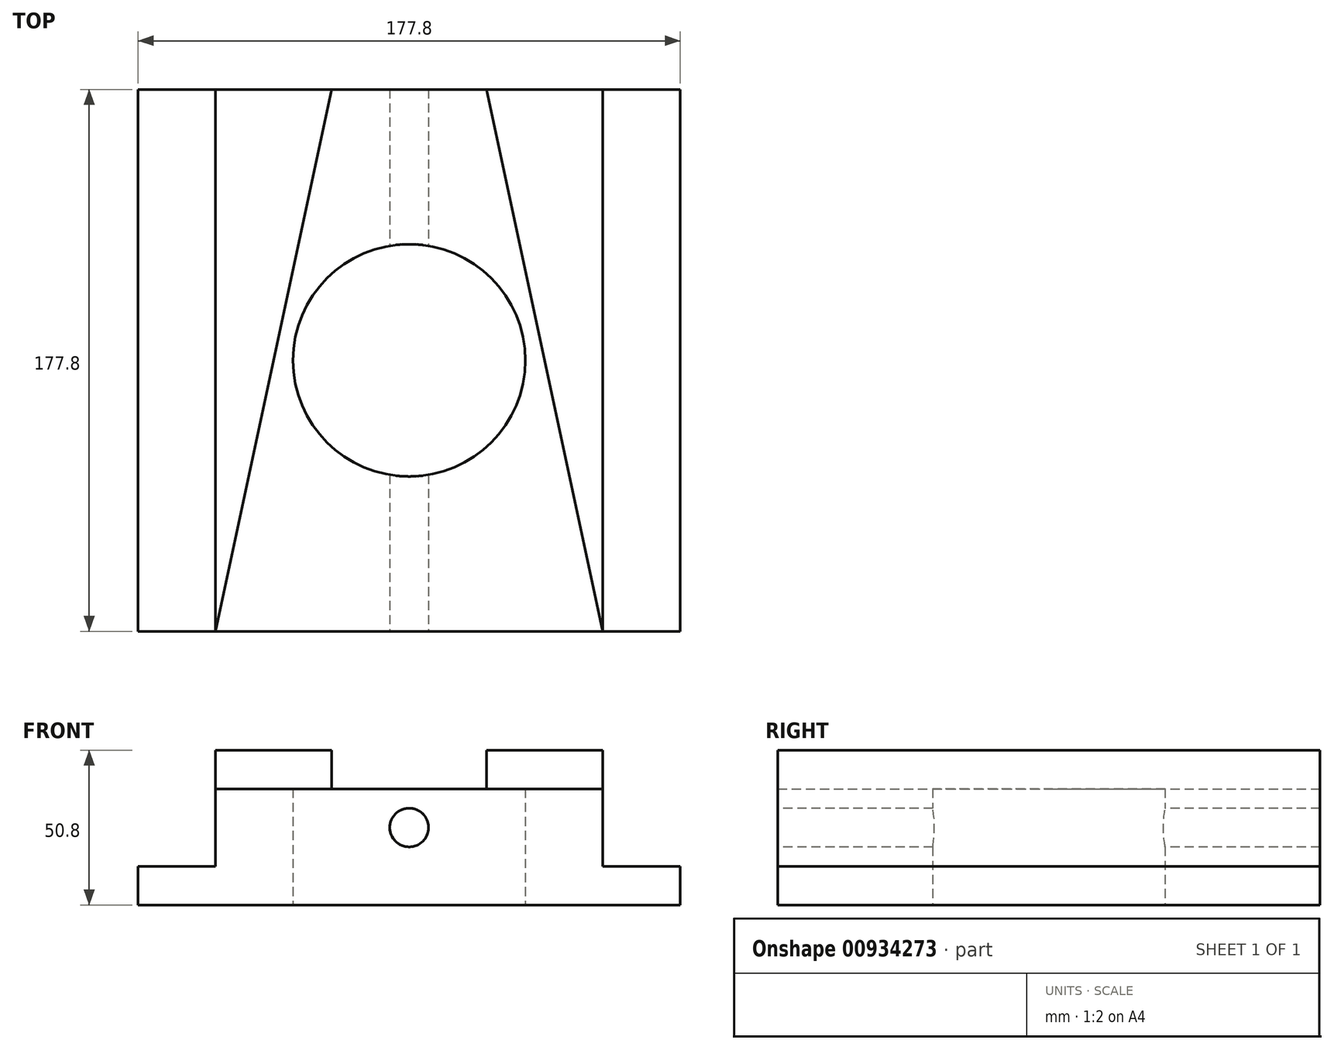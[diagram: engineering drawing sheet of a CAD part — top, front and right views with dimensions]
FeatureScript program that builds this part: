
annotation { "Feature Type Name" : "Feature", "Feature Type Description" : "" }
export const myFeature = defineFeature(function(context is Context, id is Id, definition is map)
    precondition{}
    {
        {
            var Q0;
            Q0=qCreatedBy(makeId("Top.planeOp"),FACE);
            var sketch = newSketch(context, id + "F0", { "sketchPlane" : qUnion([Q0])});
            skLineSegment(sketch, "E0.bottom", {"start": v(88.9, -88.9) * mm, "end": v(-88.9, -88.9) * mm});
            skLineSegment(sketch, "E0.top", {"start": v(88.9, 88.9) * mm, "end": v(-88.9, 88.9) * mm});
            skLineSegment(sketch, "E0.left", {"start": v(88.9, -88.9) * mm, "end": v(88.9, 88.9) * mm});
            skLineSegment(sketch, "E0.right", {"start": v(-88.9, -88.9) * mm, "end": v(-88.9, 88.9) * mm});
            skPoint(sketch, "E0.middle", {"position": v(0, 0) * mm});
            skCircle(sketch, "E1", {"center": v(0, 0) * mm, "radius": 38.1 * mm});
            skSolve(sketch);
        }
        {
            var Q0;
            Q0=makeQuery(id+"F0.imprint","IMPRINT",FACE,{"disambiguationData":[TD([[makeQuery(id+"F0.imprint","IMPRINT",EDGE,{"derivedFrom":sQuery(id+"F0.wireOp",EDGE,"E0.bottom")}),-1.0]])]});
            extrude(context, id + "F1", {"entities" : qUnion([Q0]), "depth" : 38.1 * mm, "offsetDistance" : 25.4 * mm});
        }
        {
            var Q0;
            Q0=makeQuery(id+"F1.opExtrude","CAP_FACE",FACE,{"disambiguationData":[OSD([sQuery(id+"F0.wireOp",EDGE,"E0.bottom"),sQuery(id+"F0.wireOp",EDGE,"E0.top"),sQuery(id+"F0.wireOp",EDGE,"E0.left"),sQuery(id+"F0.wireOp",EDGE,"E0.right"),sQuery(id+"F0.wireOp",EDGE,"E1")])],"isStart":false});
            var sketch = newSketch(context, id + "F2", { "sketchPlane" : qUnion([Q0])});
            skLineSegment(sketch, "E2.bottom", {"start": v(-63.5, 88.9) * mm, "end": v(63.5, 88.9) * mm});
            skLineSegment(sketch, "E2.top", {"start": v(-63.5, -88.9) * mm, "end": v(63.5, -88.9) * mm});
            skLineSegment(sketch, "E2.left", {"start": v(-63.5, 88.9) * mm, "end": v(-63.5, -88.9) * mm});
            skLineSegment(sketch, "E2.right", {"start": v(63.5, 88.9) * mm, "end": v(63.5, -88.9) * mm});
            skPoint(sketch, "E3", {"position": v(0, 0) * mm});
            skLineSegment(sketch, "E4", {"start": v(0, 88.9) * mm, "end": v(0, -88.9) * mm, "construction": true});
            skSolve(sketch);
        }
        {
            var Q0;
            {var subQ0=sQuery(id+"F2.wireOp",EDGE,"E2.left");Q0=makeQuery(id+"F2.imprint","IMPRINT",FACE,{"disambiguationData":[TD([[makeQuery(id+"F2.imprint","IMPRINT",EDGE,{"derivedFrom":subQ0}),-1.0]])]});}
            var Q1;
            {var subQ0=sQuery(id+"F2.wireOp",EDGE,"E2.right");Q1=makeQuery(id+"F2.imprint","IMPRINT",FACE,{"disambiguationData":[TD([[makeQuery(id+"F2.imprint","IMPRINT",EDGE,{"derivedFrom":subQ0}),1.0]])]});}
            extrude(context, id + "F3", {"entities" : qUnion([Q0, Q1]), "operationType" : NewBodyOperationType.REMOVE, "oppositeDirection" : true, "depth" : 25.4 * mm, "offsetDistance" : 25.4 * mm});
        }
        {
            var Q0;
            Q0=makeQuery(id+"F1.opExtrude","SWEPT_FACE",FACE,{"disambiguationData":[OSD([sQuery(id+"F0.wireOp",EDGE,"E0.bottom")])]});
            var sketch = newSketch(context, id + "F4", { "sketchPlane" : qUnion([Q0])});
            skCircle(sketch, "E5", {"center": v(0, 25.4) * mm, "radius": 6.35 * mm});
            skPoint(sketch, "E5.centerSnap0", {"position": v(-63.5, 25.4) * mm});
            skPoint(sketch, "E5.centerSnap1", {"position": v(0, 38.1) * mm});
            skSolve(sketch);
        }
        {
            var Q0;
            Q0 = qSketchRegion(id + "F4", true);
            extrude(context, id + "F5", {"entities" : qUnion([Q0]), "operationType" : NewBodyOperationType.REMOVE, "endBound" : BoundingType.THROUGH_ALL, "oppositeDirection" : true, "depth" : 25.4 * mm, "offsetDistance" : 25.4 * mm});
        }
        {
            var Q0;
            Q0=makeQuery(id+"F1.opExtrude","CAP_FACE",FACE,{"disambiguationData":[OSD([sQuery(id+"F0.wireOp",EDGE,"E0.bottom"),sQuery(id+"F0.wireOp",EDGE,"E0.top"),sQuery(id+"F0.wireOp",EDGE,"E0.left"),sQuery(id+"F0.wireOp",EDGE,"E0.right"),sQuery(id+"F0.wireOp",EDGE,"E1")])],"isStart":false});
            var sketch = newSketch(context, id + "F6", { "sketchPlane" : qUnion([Q0])});
            skLineSegment(sketch, "E6", {"start": v(-25.4, 88.9) * mm, "end": v(-63.5, -88.9) * mm});
            skLineSegment(sketch, "E7", {"start": v(-63.5, -88.9) * mm, "end": v(63.5, -88.9) * mm});
            skLineSegment(sketch, "E8", {"start": v(63.5, -88.9) * mm, "end": v(25.4, 88.9) * mm});
            skLineSegment(sketch, "E9", {"start": v(25.4, 88.9) * mm, "end": v(-25.4, 88.9) * mm});
            skLineSegment(sketch, "E10", {"start": v(0, 88.9) * mm, "end": v(0, -88.9) * mm, "construction": true});
            skSolve(sketch);
        }
        {
            var Q0;
            {var subQ0=sQuery(id+"F6.wireOp",EDGE,"E8");Q0=makeQuery(id+"F6.imprint","IMPRINT",FACE,{"disambiguationData":[TD([[makeQuery(id+"F6.imprint","IMPRINT",EDGE,{"derivedFrom":subQ0}),-1.0]])]});}
            var Q1;
            {var subQ0=sQuery(id+"F6.wireOp",EDGE,"E6");Q1=makeQuery(id+"F6.imprint","IMPRINT",FACE,{"disambiguationData":[TD([[makeQuery(id+"F6.imprint","IMPRINT",EDGE,{"derivedFrom":subQ0}),-1.0]])]});}
            extrude(context, id + "F7", {"entities" : qUnion([Q0, Q1]), "operationType" : NewBodyOperationType.ADD, "depth" : 12.7 * mm, "offsetDistance" : 25.4 * mm});
        }
    });
